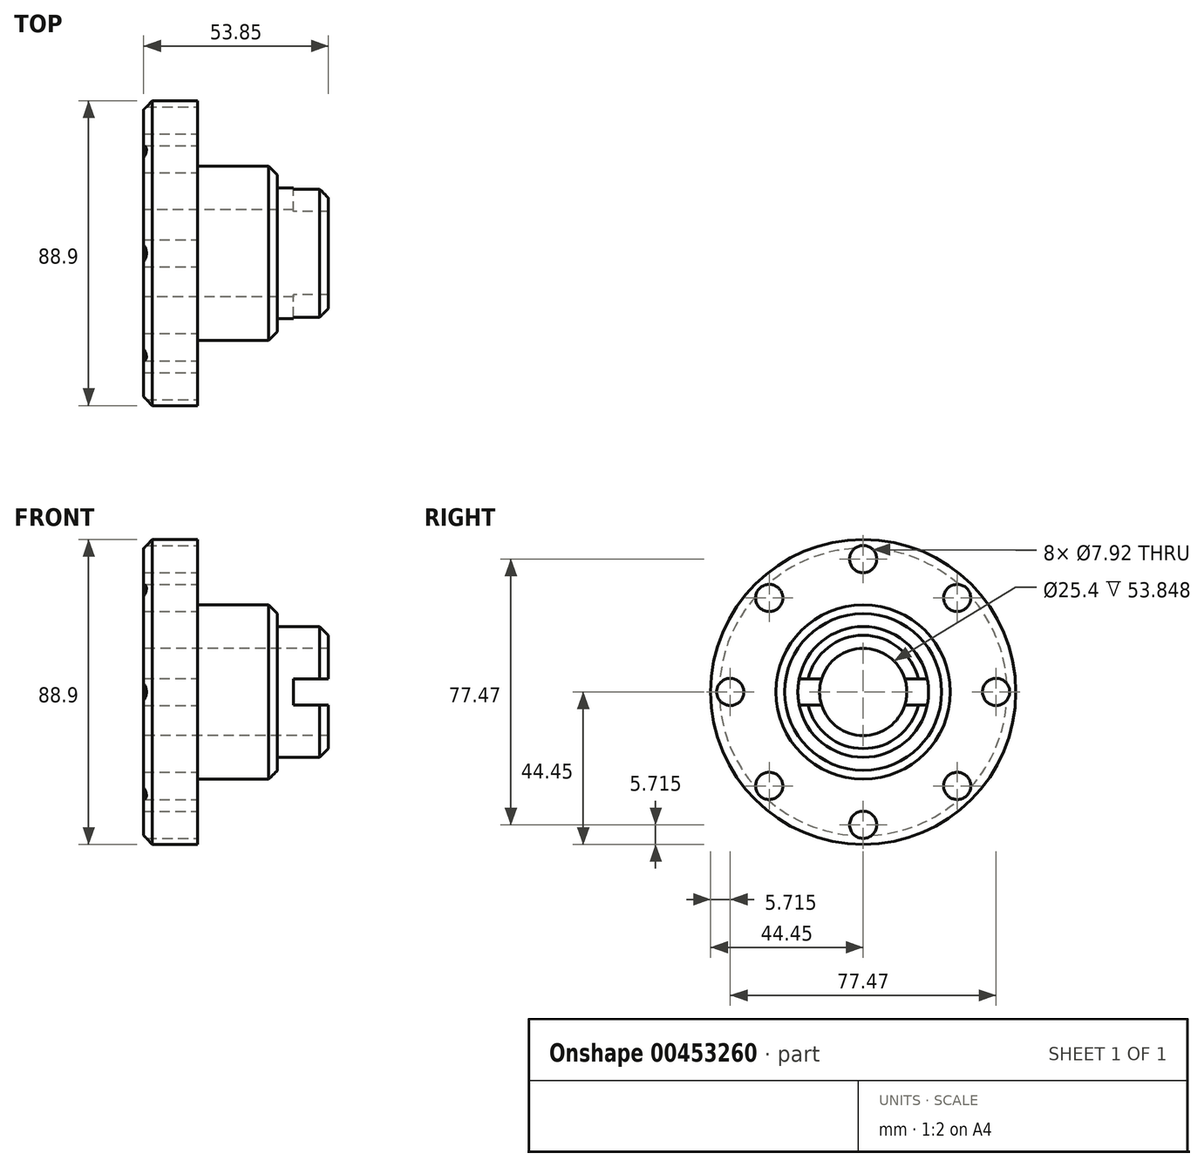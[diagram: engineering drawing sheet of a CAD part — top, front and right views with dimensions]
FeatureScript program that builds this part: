
annotation { "Feature Type Name" : "Feature", "Feature Type Description" : "" }
export const myFeature = defineFeature(function(context is Context, id is Id, definition is map)
    precondition{}
    {
        {
            var Q0;
            Q0=qCreatedBy(makeId("Top.planeOp"),FACE);
            var sketch = newSketch(context, id + "F0", { "sketchPlane" : qUnion([Q0])});
            skLineSegment(sketch, "E0", {"start": v(0, 44.45) * mm, "end": v(0, 25.4) * mm});
            skLineSegment(sketch, "E1", {"start": v(0, 25.4) * mm, "end": v(23.24, 25.4) * mm});
            skLineSegment(sketch, "E2", {"start": v(23.24, 25.4) * mm, "end": v(23.24, 19.05) * mm});
            skLineSegment(sketch, "E3", {"start": v(23.24, 19.05) * mm, "end": v(38.1, 19.05) * mm});
            skLineSegment(sketch, "E4", {"start": v(38.1, 19.05) * mm, "end": v(38.1, 12.7) * mm});
            skLineSegment(sketch, "E5", {"start": v(38.1, 12.7) * mm, "end": v(-15.75, 12.7) * mm});
            skLineSegment(sketch, "E6", {"start": v(-15.75, 12.7) * mm, "end": v(-15.75, 44.45) * mm});
            skLineSegment(sketch, "E7", {"start": v(-15.75, 44.45) * mm, "end": v(0, 44.45) * mm});
            skLineSegment(sketch, "E8", {"start": v(0, 0) * mm, "end": v(152.4, 0) * mm, "construction": true});
            skSolve(sketch);
        }
        {
            var Q0;
            Q0=makeQuery(id+"F0.imprint","IMPRINT",FACE,{"disambiguationData":[TD([[makeQuery(id+"F0.imprint","IMPRINT",EDGE,{"derivedFrom":sQuery(id+"F0.wireOp",EDGE,"E0")}),-1.0]])]});
            var Q1;
            Q1=sQuery(id+"F0.wireOp",EDGE,"E8");
            revolve(context, id + "F1", {"entities" : qUnion([Q0]), "axis" : qUnion([Q1]), "revolveType" : RevolveType.FULL});
        }
        {
            var Q0;
            Q0=makeQuery(id+"F1.opRevolve","SWEPT_EDGE",EDGE,{"disambiguationData":[OSD([sQuery(id+"F0.wireOp",EDGE,"E3"),sQuery(id+"F0.wireOp",EDGE,"E4")])]});
            var Q1;
            Q1=makeQuery(id+"F1.opRevolve","SWEPT_EDGE",EDGE,{"disambiguationData":[OSD([sQuery(id+"F0.wireOp",EDGE,"E1"),sQuery(id+"F0.wireOp",EDGE,"E2")])]});
            var Q2;
            Q2=makeQuery(id+"F1.opRevolve","SWEPT_EDGE",EDGE,{"disambiguationData":[OSD([sQuery(id+"F0.wireOp",EDGE,"E6"),sQuery(id+"F0.wireOp",EDGE,"E7")])]});
            chamfer(context, id + "F2", {"entities" : qUnion([Q0, Q1, Q2]), "width" : 2.54 * mm, "tangentPropagation" : true});
        }
        {
            var Q0;
            Q0=qCreatedBy(makeId("Front.planeOp"),FACE);
            var sketch = newSketch(context, id + "F3", { "sketchPlane" : qUnion([Q0])});
            skLineSegment(sketch, "E9.bottom", {"start": v(78.74, -3.8) * mm, "end": v(27.94, -3.8) * mm});
            skLineSegment(sketch, "E9.top", {"start": v(78.74, 3.81) * mm, "end": v(27.94, 3.81) * mm});
            skLineSegment(sketch, "E9.left", {"start": v(78.74, -3.8) * mm, "end": v(78.74, 3.81) * mm});
            skLineSegment(sketch, "E9.right", {"start": v(27.94, -3.8) * mm, "end": v(27.94, 3.81) * mm});
            skSolve(sketch);
        }
        {
            var Q0;
            Q0=makeQuery(id+"F3.imprint","IMPRINT",FACE,{"disambiguationData":[TD([[makeQuery(id+"F3.imprint","IMPRINT",EDGE,{"derivedFrom":sQuery(id+"F3.wireOp",EDGE,"E9.bottom")}),-1.0]])]});
            extrude(context, id + "F4", {"entities" : qUnion([Q0]), "depth" : 85.34 * mm, "symmetric" : true});
        }
        {
            var Q0;
            Q0=makeQuery(id+"F4.opExtrude","SWEPT_BODY",BODY,{"disambiguationData":[OSD([sQuery(id+"F3.wireOp",EDGE,"E9.bottom"),sQuery(id+"F3.wireOp",EDGE,"E9.top"),sQuery(id+"F3.wireOp",EDGE,"E9.left"),sQuery(id+"F3.wireOp",EDGE,"E9.right")])]});
            var Q1;
            Q1=makeQuery(id+"F1.opRevolve","SWEPT_BODY",BODY,{"disambiguationData":[OSD([sQuery(id+"F0.wireOp",EDGE,"E0"),sQuery(id+"F0.wireOp",EDGE,"E1"),sQuery(id+"F0.wireOp",EDGE,"E2"),sQuery(id+"F0.wireOp",EDGE,"E3"),sQuery(id+"F0.wireOp",EDGE,"E4"),sQuery(id+"F0.wireOp",EDGE,"E5"),sQuery(id+"F0.wireOp",EDGE,"E6"),sQuery(id+"F0.wireOp",EDGE,"E7")])]});
            booleanBodies(context, id + "F5", {"operationType" : BooleanOperationType.SUBTRACTION, "tools" : qUnion([Q0]), "targets" : qUnion([Q1])});
        }
        {
            var Q0;
            Q0=makeQuery(id+"F1.opRevolve","SWEPT_FACE",FACE,{"disambiguationData":[OSD([sQuery(id+"F0.wireOp",EDGE,"E0")])]});
            var sketch = newSketch(context, id + "F6", { "sketchPlane" : qUnion([Q0])});
            skCircle(sketch, "E10", {"center": v(0, -38.73) * mm, "radius": 3.96 * mm});
            skSolve(sketch);
        }
        {
            var Q0;
            Q0=makeQuery(id+"F6.imprint","IMPRINT",FACE,{"disambiguationData":[TD([[makeQuery(id+"F6.imprint","IMPRINT",EDGE,{"derivedFrom":sQuery(id+"F6.wireOp",EDGE,"E10")}),1.0]])]});
            extrude(context, id + "F7", {"entities" : qUnion([Q0]), "oppositeDirection" : true, "depth" : 38.6 * mm, "hasSecondDirection" : true, "secondDirectionOppositeDirection" : false, "secondDirectionDepth" : 9.4 * mm});
        }
        {
            var Q0;
            Q0=makeQuery(id+"F7.opExtrude","SWEPT_BODY",BODY,{"disambiguationData":[OSD([sQuery(id+"F6.wireOp",EDGE,"E10")])]});
            var Q1;
            Q1=makeQuery(id+"F1.opRevolve","SWEPT_FACE",FACE,{"disambiguationData":[OSD([sQuery(id+"F0.wireOp",EDGE,"E5")])]});
            circularPattern(context, id + "F8", {"entities" : qUnion([Q0]), "axis" : qUnion([Q1]), "angle" : 360 * degree, "instanceCount" : 8, "equalSpace" : true});
        }
        {
            var Q0;
            Q0=makeQuery(id+"F8.opPattern","COPY",BODY,{"derivedFrom":makeQuery(id+"F7.opExtrude","SWEPT_BODY",BODY,{"disambiguationData":[OSD([sQuery(id+"F6.wireOp",EDGE,"E10")])]}),"instanceName":"5"});
            var Q1;
            Q1=makeQuery(id+"F7.opExtrude","SWEPT_BODY",BODY,{"disambiguationData":[OSD([sQuery(id+"F6.wireOp",EDGE,"E10")])]});
            var Q2;
            Q2=makeQuery(id+"F8.opPattern","COPY",BODY,{"derivedFrom":makeQuery(id+"F7.opExtrude","SWEPT_BODY",BODY,{"disambiguationData":[OSD([sQuery(id+"F6.wireOp",EDGE,"E10")])]}),"instanceName":"1"});
            var Q3;
            Q3=makeQuery(id+"F8.opPattern","COPY",BODY,{"derivedFrom":makeQuery(id+"F7.opExtrude","SWEPT_BODY",BODY,{"disambiguationData":[OSD([sQuery(id+"F6.wireOp",EDGE,"E10")])]}),"instanceName":"4"});
            var Q4;
            Q4=makeQuery(id+"F8.opPattern","COPY",BODY,{"derivedFrom":makeQuery(id+"F7.opExtrude","SWEPT_BODY",BODY,{"disambiguationData":[OSD([sQuery(id+"F6.wireOp",EDGE,"E10")])]}),"instanceName":"7"});
            var Q5;
            Q5=makeQuery(id+"F8.opPattern","COPY",BODY,{"derivedFrom":makeQuery(id+"F7.opExtrude","SWEPT_BODY",BODY,{"disambiguationData":[OSD([sQuery(id+"F6.wireOp",EDGE,"E10")])]}),"instanceName":"6"});
            var Q6;
            Q6=makeQuery(id+"F8.opPattern","COPY",BODY,{"derivedFrom":makeQuery(id+"F7.opExtrude","SWEPT_BODY",BODY,{"disambiguationData":[OSD([sQuery(id+"F6.wireOp",EDGE,"E10")])]}),"instanceName":"2"});
            var Q7;
            Q7=makeQuery(id+"F8.opPattern","COPY",BODY,{"derivedFrom":makeQuery(id+"F7.opExtrude","SWEPT_BODY",BODY,{"disambiguationData":[OSD([sQuery(id+"F6.wireOp",EDGE,"E10")])]}),"instanceName":"3"});
            var Q8;
            Q8=makeQuery(id+"F1.opRevolve","SWEPT_BODY",BODY,{"disambiguationData":[OSD([sQuery(id+"F0.wireOp",EDGE,"E0"),sQuery(id+"F0.wireOp",EDGE,"E1"),sQuery(id+"F0.wireOp",EDGE,"E2"),sQuery(id+"F0.wireOp",EDGE,"E3"),sQuery(id+"F0.wireOp",EDGE,"E4"),sQuery(id+"F0.wireOp",EDGE,"E5"),sQuery(id+"F0.wireOp",EDGE,"E6"),sQuery(id+"F0.wireOp",EDGE,"E7")])]});
            booleanBodies(context, id + "F9", {"operationType" : BooleanOperationType.SUBTRACTION, "tools" : qUnion([Q0, Q1, Q2, Q3, Q4, Q5, Q6, Q7]), "targets" : qUnion([Q8])});
        }
    });
